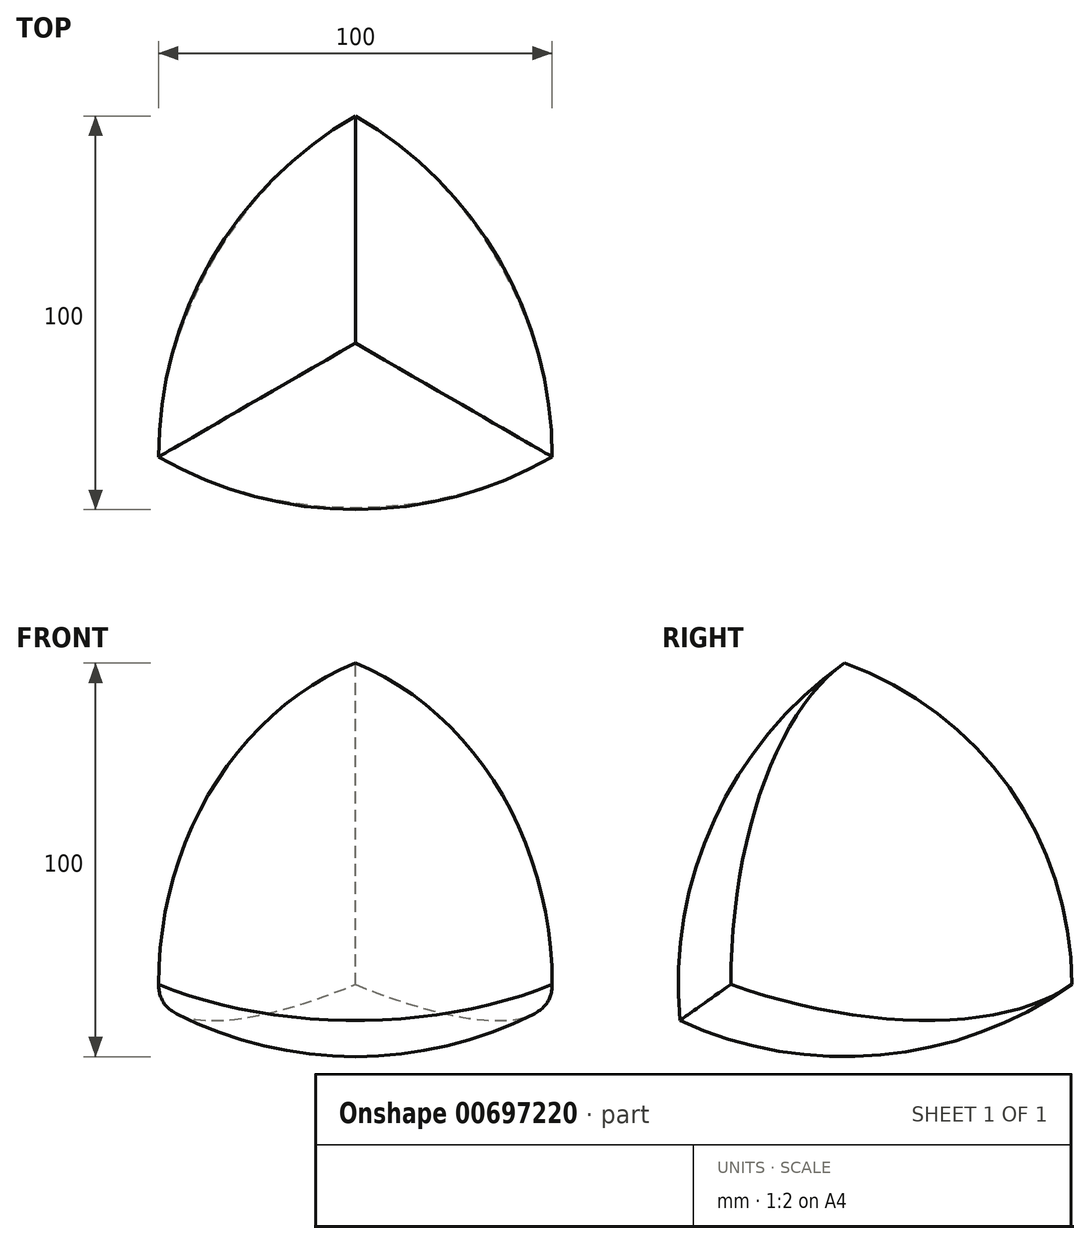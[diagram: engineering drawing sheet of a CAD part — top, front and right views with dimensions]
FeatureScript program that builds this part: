
annotation { "Feature Type Name" : "Feature", "Feature Type Description" : "" }
export const myFeature = defineFeature(function(context is Context, id is Id, definition is map)
    precondition{}
    {
        {
            var Q0;
            Q0=qCreatedBy(makeId("Top.planeOp"),FACE);
            var sketch = newSketch(context, id + "F0", { "sketchPlane" : qUnion([Q0])});
            skCircle(sketch, "E0.cCircle", {"center": v(0, 0) * mm, "radius": 28.87 * mm, "construction": true});
            skLineSegment(sketch, "E0.0", {"start": v(0, 57.74) * mm, "end": v(50, -28.87) * mm, "construction": true});
            skLineSegment(sketch, "E0.1", {"start": v(50, -28.87) * mm, "end": v(-50, -28.87) * mm, "construction": true});
            skLineSegment(sketch, "E0.2", {"start": v(-50, -28.87) * mm, "end": v(0, 57.74) * mm, "construction": true});
            skPoint(sketch, "E0.0.midPoint", {"position": v(25, 14.43) * mm});
            skSolve(sketch);
        }
        {
            var Q0;
            Q0=qCreatedBy(makeId("Right.planeOp"),FACE);
            var sketch = newSketch(context, id + "F1", { "sketchPlane" : qUnion([Q0])});
            skLineSegment(sketch, "E1", {"start": v(0, 0) * mm, "end": v(0, 81.65) * mm, "construction": true});
            skSolve(sketch);
        }
        {
            var Q0;
            Q0=sQuery(id+"F0.wireOp",VERTEX,"E0.1.start");
            var Q1;
            Q1=sQuery(id+"F1.wireOp",VERTEX,"E1.end");
            var Q2;
            Q2=sQuery(id+"F0.wireOp",VERTEX,"E0.0.start");
            cPlane(context, id + "F2", {"entities" : qUnion([Q0, Q1, Q2]), "cplaneType" : CPlaneType.THREE_POINT, "offset" : 25 * mm, "width" : 150 * mm, "height" : 150 * mm});
        }
        {
            var Q0;
            Q0=qCreatedBy(id+"F2.planeOp",FACE);
            var sketch = newSketch(context, id + "F3", { "sketchPlane" : qUnion([Q0])});
            skLineSegment(sketch, "E2", {"start": v(50.92, 0) * mm, "end": v(-14.55, 75.6) * mm, "construction": true});
            skLineSegment(sketch, "E3", {"start": v(-14.55, 75.6) * mm, "end": v(-47.28, -18.9) * mm, "construction": true});
            skSolve(sketch);
        }
        {
            var Q0;
            Q0=sQuery(id+"F0.wireOp",VERTEX,"E0.2.start");
            var Q1;
            Q1=sQuery(id+"F0.wireOp",VERTEX,"E0.0.end");
            var Q2;
            Q2=sQuery(id+"F3.wireOp",VERTEX,"E3.start");
            cPlane(context, id + "F4", {"entities" : qUnion([Q0, Q1, Q2]), "cplaneType" : CPlaneType.THREE_POINT, "offset" : 25 * mm, "width" : 150 * mm, "height" : 150 * mm});
        }
        {
            var Q0;
            Q0=qCreatedBy(id+"F4.planeOp",FACE);
            var sketch = newSketch(context, id + "F5", { "sketchPlane" : qUnion([Q0])});
            skLineSegment(sketch, "E4", {"start": v(50, -9.62) * mm, "end": v(0, 76.98) * mm, "construction": true});
            skSolve(sketch);
        }
        {
            var Q0;
            Q0=sQuery(id+"F5.wireOp",VERTEX,"E4.start");
            var Q1;
            Q1=sQuery(id+"F0.wireOp",VERTEX,"E0.0.midPoint");
            var Q2;
            Q2=sQuery(id+"F5.wireOp",VERTEX,"E4.end");
            cPlane(context, id + "F6", {"entities" : qUnion([Q0, Q1, Q2]), "cplaneType" : CPlaneType.THREE_POINT, "offset" : 25 * mm, "width" : 150 * mm, "height" : 150 * mm});
        }
        {
            var Q0;
            Q0=qCreatedBy(id+"F6.planeOp",FACE);
            var sketch = newSketch(context, id + "F7", { "sketchPlane" : qUnion([Q0])});
            skArc(sketch, "E5", {"start": v(0, 81.65) * mm, "mid": v(-23.91, -57.74) * mm, "end": v(115.47, -81.65) * mm});
            skLineSegment(sketch, "E6", {"start": v(0, 81.65) * mm, "end": v(115.47, -81.65) * mm});
            skSolve(sketch);
        }
        {
            var Q0;
            Q0=sQuery(id+"F0.wireOp",EDGE,"E0.1");
            cPoint(context, id + "F8", {"entities" : qUnion([Q0]), "parameter" : 0.5});
        }
        {
            var Q0;
            Q0 = qCreatedBy(id + "F8" ,VERTEX);
            var Q1;
            Q1=sQuery(id+"F7.wireOp",VERTEX,"E5.start");
            var Q2;
            Q2=sQuery(id+"F0.wireOp",VERTEX,"E0.0.start");
            cPlane(context, id + "F9", {"entities" : qUnion([Q0, Q1, Q2]), "cplaneType" : CPlaneType.THREE_POINT, "offset" : 25 * mm, "width" : 150 * mm, "height" : 150 * mm});
        }
        {
            var Q0;
            Q0=qCreatedBy(id+"F9.planeOp",FACE);
            var sketch = newSketch(context, id + "F10", { "sketchPlane" : qUnion([Q0])});
            skArc(sketch, "E7", {"start": v(0, 81.65) * mm, "mid": v(-23.91, -57.74) * mm, "end": v(115.47, -81.65) * mm});
            skLineSegment(sketch, "E8", {"start": v(115.47, -81.65) * mm, "end": v(0, 81.65) * mm});
            skSolve(sketch);
        }
        {
            var Q0;
            Q0=sQuery(id+"F0.wireOp",EDGE,"E0.2");
            cPoint(context, id + "F11", {"entities" : qUnion([Q0]), "parameter" : 0.5});
        }
        {
            var Q0;
            Q0=sQuery(id+"F10.wireOp",VERTEX,"E7.start");
            var Q1;
            Q1=sQuery(id+"F0.wireOp",VERTEX,"E0.0.end");
            var Q2;
            Q2 = qCreatedBy(id + "F11" ,VERTEX);
            cPlane(context, id + "F12", {"entities" : qUnion([Q0, Q1, Q2]), "cplaneType" : CPlaneType.THREE_POINT, "offset" : 25 * mm, "width" : 150 * mm, "height" : 150 * mm});
        }
        {
            var Q0;
            Q0=qCreatedBy(id+"F12.planeOp",FACE);
            var sketch = newSketch(context, id + "F13", { "sketchPlane" : qUnion([Q0])});
            skArc(sketch, "E9", {"start": v(0, 81.65) * mm, "mid": v(-23.91, -57.74) * mm, "end": v(115.47, -81.65) * mm});
            skLineSegment(sketch, "E10", {"start": v(115.47, -81.65) * mm, "end": v(0, 81.65) * mm});
            skSolve(sketch);
        }
        {
            var Q0;
            Q0=sQuery(id+"F0.wireOp",EDGE,"E0.1");
            cPoint(context, id + "F14", {"entities" : qUnion([Q0]), "parameter" : 0.5});
        }
        {
            var Q0;
            Q0=sQuery(id+"F10.wireOp",VERTEX,"E7.center");
            var Q1;
            Q1=sQuery(id+"F13.wireOp",VERTEX,"E9.start");
            var Q2;
            Q2 = qCreatedBy(id + "F14" ,VERTEX);
            cPlane(context, id + "F15", {"entities" : qUnion([Q0, Q1, Q2]), "cplaneType" : CPlaneType.THREE_POINT, "offset" : 25 * mm, "width" : 150 * mm, "height" : 150 * mm});
        }
        {
            var Q0;
            Q0=qCreatedBy(id+"F15.planeOp",FACE);
            var sketch = newSketch(context, id + "F16", { "sketchPlane" : qUnion([Q0])});
            skArc(sketch, "E11", {"start": v(-57.74, 0) * mm, "mid": v(81.65, 23.91) * mm, "end": v(57.74, 163.3) * mm});
            skLineSegment(sketch, "E12", {"start": v(-57.74, 0) * mm, "end": v(57.74, 163.3) * mm});
            skSolve(sketch);
        }
        {
            var Q0;
            Q0=makeQuery(id+"F10.imprint","IMPRINT",FACE,{"disambiguationData":[TD([[makeQuery(id+"F10.imprint","IMPRINT",EDGE,{"derivedFrom":sQuery(id+"F10.wireOp",EDGE,"E7")}),1.0]])]});
            var Q1;
            Q1=sQuery(id+"F10.wireOp",EDGE,"E7");
            var Q2;
            Q2=sQuery(id+"F10.wireOp",EDGE,"E8");
            revolve(context, id + "F17", {"entities" : qUnion([Q0]), "surfaceEntities" : qUnion([Q1]), "axis" : qUnion([Q2]), "revolveType" : RevolveType.FULL});
        }
        {
            var Q0;
            Q0=makeQuery(id+"F16.imprint","IMPRINT",FACE,{"disambiguationData":[TD([[makeQuery(id+"F16.imprint","IMPRINT",EDGE,{"derivedFrom":sQuery(id+"F16.wireOp",EDGE,"E11")}),1.0]])]});
            var Q1;
            Q1=sQuery(id+"F16.wireOp",EDGE,"E11");
            var Q2;
            Q2=sQuery(id+"F16.wireOp",EDGE,"E12");
            revolve(context, id + "F18", {"entities" : qUnion([Q0]), "surfaceEntities" : qUnion([Q1]), "axis" : qUnion([Q2]), "revolveType" : RevolveType.FULL});
        }
        {
            var Q0;
            Q0=makeQuery(id+"F7.imprint","IMPRINT",FACE,{"disambiguationData":[TD([[makeQuery(id+"F7.imprint","IMPRINT",EDGE,{"derivedFrom":sQuery(id+"F7.wireOp",EDGE,"E5")}),1.0]])]});
            var Q1;
            Q1=sQuery(id+"F7.wireOp",EDGE,"E5");
            var Q2;
            Q2=sQuery(id+"F7.wireOp",EDGE,"E6");
            revolve(context, id + "F19", {"entities" : qUnion([Q0]), "surfaceEntities" : qUnion([Q1]), "axis" : qUnion([Q2]), "revolveType" : RevolveType.FULL});
        }
        {
            var Q0;
            Q0=makeQuery(id+"F13.imprint","IMPRINT",FACE,{"disambiguationData":[TD([[makeQuery(id+"F13.imprint","IMPRINT",EDGE,{"derivedFrom":sQuery(id+"F13.wireOp",EDGE,"E9")}),1.0]])]});
            var Q1;
            Q1=sQuery(id+"F13.wireOp",EDGE,"E9");
            var Q2;
            Q2=sQuery(id+"F13.wireOp",EDGE,"E10");
            revolve(context, id + "F20", {"entities" : qUnion([Q0]), "surfaceEntities" : qUnion([Q1]), "axis" : qUnion([Q2]), "revolveType" : RevolveType.FULL});
        }
        {
            var Q0;
            Q0=makeQuery(id+"F18.opRevolve","SWEPT_BODY",BODY,{"disambiguationData":[OSD([sQuery(id+"F16.wireOp",EDGE,"E11"),sQuery(id+"F16.wireOp",EDGE,"E12")])]});
            var Q1;
            Q1=makeQuery(id+"F19.opRevolve","SWEPT_BODY",BODY,{"disambiguationData":[OSD([sQuery(id+"F7.wireOp",EDGE,"E5"),sQuery(id+"F7.wireOp",EDGE,"E6")])]});
            var Q2;
            Q2=makeQuery(id+"F20.opRevolve","SWEPT_BODY",BODY,{"disambiguationData":[OSD([sQuery(id+"F13.wireOp",EDGE,"E9"),sQuery(id+"F13.wireOp",EDGE,"E10")])]});
            var Q3;
            Q3=makeQuery(id+"F17.opRevolve","SWEPT_BODY",BODY,{"disambiguationData":[OSD([sQuery(id+"F10.wireOp",EDGE,"E7"),sQuery(id+"F10.wireOp",EDGE,"E8")])]});
            booleanBodies(context, id + "F21", {"operationType" : BooleanOperationType.INTERSECTION, "tools" : qUnion([Q0, Q1, Q2, Q3])});
        }
        {
            var Q0;
            Q0=sQuery(id+"F3.wireOp",VERTEX,"E3.start");
            var Q1;
            Q1=sQuery(id+"F0.wireOp",VERTEX,"E0.2.start");
            var Q2;
            Q2=sQuery(id+"F0.wireOp",VERTEX,"E0.2.end");
            cPlane(context, id + "F22", {"entities" : qUnion([Q0, Q1, Q2]), "cplaneType" : CPlaneType.THREE_POINT, "offset" : 25 * mm, "width" : 150 * mm, "height" : 150 * mm});
        }
    });
